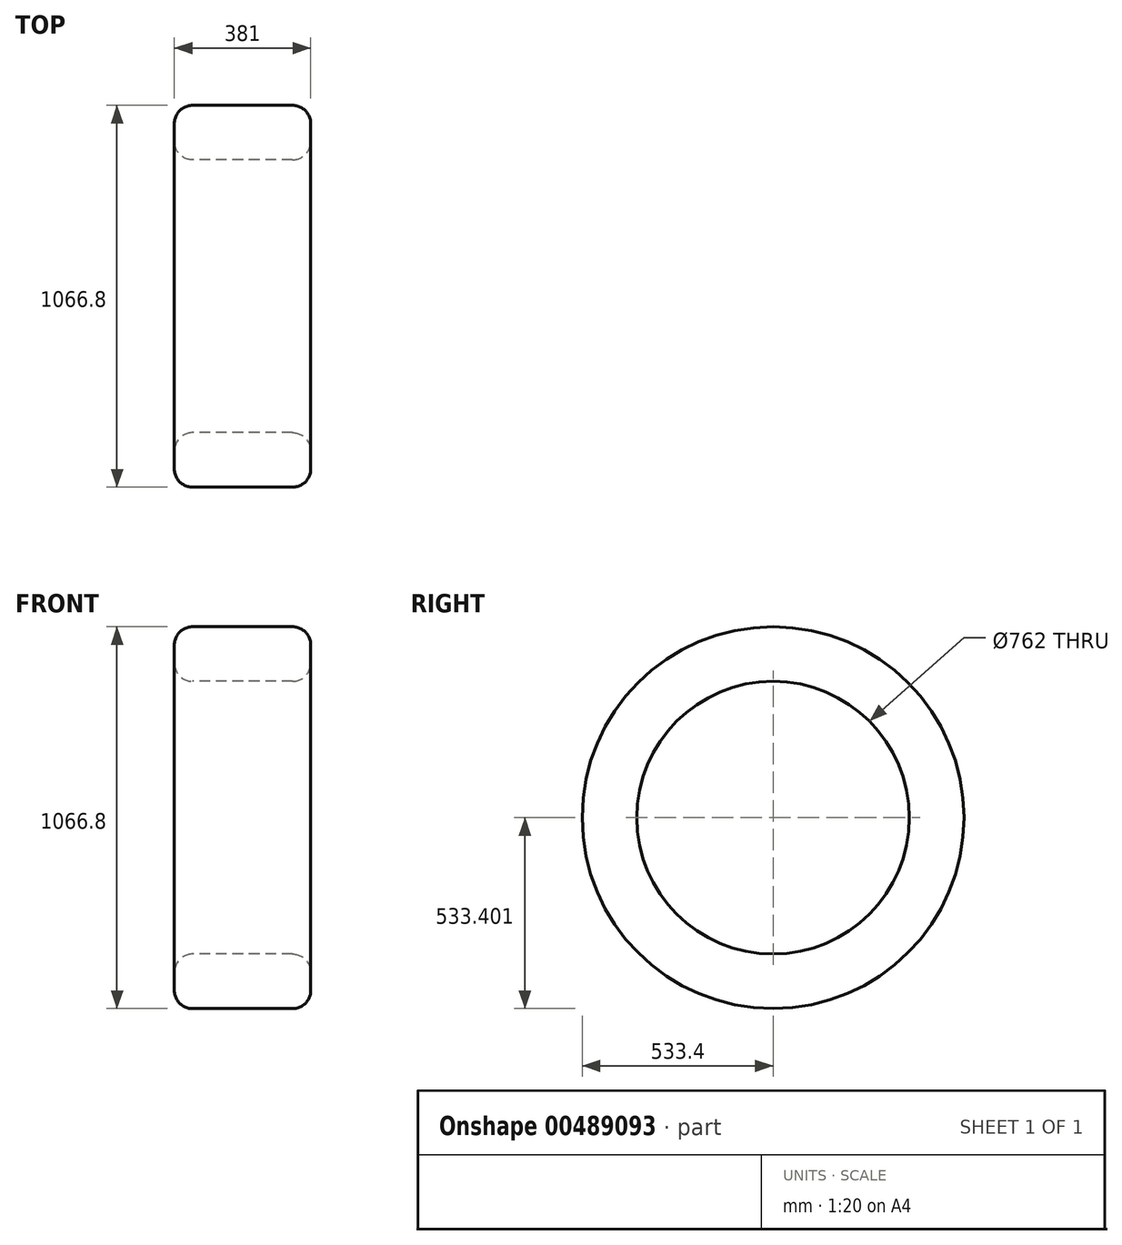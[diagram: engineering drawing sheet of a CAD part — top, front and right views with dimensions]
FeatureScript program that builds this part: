
annotation { "Feature Type Name" : "Feature", "Feature Type Description" : "" }
export const myFeature = defineFeature(function(context is Context, id is Id, definition is map)
    precondition{}
    {
        {
            var Q0;
            Q0=qCreatedBy(makeId("Front.planeOp"),FACE);
            var sketch = newSketch(context, id + "F0", { "sketchPlane" : qUnion([Q0])});
            skLineSegment(sketch, "E0.bottom", {"start": v(-5.87, 169.93) * mm, "end": v(273.53, 169.93) * mm});
            skLineSegment(sketch, "E0.top", {"start": v(-5.87, 17.53) * mm, "end": v(273.53, 17.53) * mm});
            skLineSegment(sketch, "E0.left", {"start": v(-56.67, 119.13) * mm, "end": v(-56.67, 68.33) * mm});
            skLineSegment(sketch, "E0.right", {"start": v(324.33, 119.13) * mm, "end": v(324.33, 68.33) * mm});
            skPoint(sketch, "E1.visualSharp", {"position": v(-56.67, 169.93) * mm});
            skArc(sketch, "E1.filletArc", {"start": v(-5.87, 169.93) * mm, "mid": v(-41.79, 155.05) * mm, "end": v(-56.67, 119.13) * mm});
            skPoint(sketch, "E2.visualSharp", {"position": v(-56.67, 17.53) * mm});
            skArc(sketch, "E2.filletArc", {"start": v(-56.67, 68.33) * mm, "mid": v(-41.79, 32.4) * mm, "end": v(-5.87, 17.53) * mm});
            skPoint(sketch, "E3.visualSharp", {"position": v(324.33, 17.53) * mm});
            skArc(sketch, "E3.filletArc", {"start": v(273.53, 17.53) * mm, "mid": v(309.45, 32.4) * mm, "end": v(324.33, 68.33) * mm});
            skPoint(sketch, "E4.visualSharp", {"position": v(324.33, 169.93) * mm});
            skArc(sketch, "E4.filletArc", {"start": v(324.33, 119.13) * mm, "mid": v(309.45, 155.05) * mm, "end": v(273.53, 169.93) * mm});
            skLineSegment(sketch, "E5", {"start": v(-76.55, -363.47) * mm, "end": v(304.45, -363.47) * mm});
            skSolve(sketch);
        }
        {
            var Q0;
            Q0=makeQuery(id+"F0.imprint","IMPRINT",FACE,{"disambiguationData":[TD([[makeQuery(id+"F0.imprint","IMPRINT",EDGE,{"derivedFrom":sQuery(id+"F0.wireOp",EDGE,"E0.bottom")}),-1.0]])]});
            var Q1;
            Q1=sQuery(id+"F0.wireOp",EDGE,"E5");
            revolve(context, id + "F1", {"entities" : qUnion([Q0]), "axis" : qUnion([Q1]), "revolveType" : RevolveType.FULL});
        }
        {
            var Q0;
            Q0=qCreatedBy(makeId("Front.planeOp"),FACE);
            var sketch = newSketch(context, id + "F2", { "sketchPlane" : qUnion([Q0])});
            skLineSegment(sketch, "E6", {"start": v(180.7, -33.27) * mm, "end": v(244.2, -33.27) * mm});
            skLineSegment(sketch, "E7", {"start": v(-20.53, -7.87) * mm, "end": v(-54.19, 50.42) * mm});
            skLineSegment(sketch, "E8", {"start": v(288.2, -7.87) * mm, "end": v(323.08, 52.55) * mm});
            skPoint(sketch, "E9.visualSharp", {"position": v(273.53, -33.27) * mm});
            skArc(sketch, "E9.filletArc", {"start": v(244.2, -33.27) * mm, "mid": v(269.6, -26.46) * mm, "end": v(288.2, -7.87) * mm});
            skPoint(sketch, "E10.visualSharp", {"position": v(-5.87, -33.27) * mm});
            skArc(sketch, "E10.filletArc", {"start": v(-20.53, -7.87) * mm, "mid": v(-1.94, -26.46) * mm, "end": v(23.46, -33.27) * mm});
            skLineSegment(sketch, "E11", {"start": v(129.9, -84.07) * mm, "end": v(129.9, -287.27) * mm});
            skArc(sketch, "E12.filletArc", {"start": v(180.7, -33.27) * mm, "mid": v(144.78, -48.15) * mm, "end": v(129.9, -84.07) * mm});
            skLineSegment(sketch, "E13", {"start": v(23.46, -33.27) * mm, "end": v(180.7, -33.27) * mm});
            skSolve(sketch);
        }
        {
            var Q0;
            Q0=sQuery(id+"F2.wireOp",EDGE,"E7");
            var Q1;
            Q1=sQuery(id+"F2.wireOp",EDGE,"E10.filletArc");
            var Q2;
            Q2=sQuery(id+"F2.wireOp",EDGE,"E13");
            var Q3;
            Q3=sQuery(id+"F2.wireOp",EDGE,"E6");
            var Q4;
            Q4=sQuery(id+"F2.wireOp",EDGE,"E9.filletArc");
            var Q5;
            Q5=sQuery(id+"F2.wireOp",EDGE,"E8");
            var Q6;
            Q6=sQuery(id+"F0.wireOp",EDGE,"E5");
            revolve(context, id + "F3", {"bodyType" : ToolBodyType.SURFACE, "surfaceEntities" : qUnion([Q0, Q1, Q2, Q3, Q4, Q5]), "axis" : qUnion([Q6]), "revolveType" : RevolveType.FULL});
        }
    });
